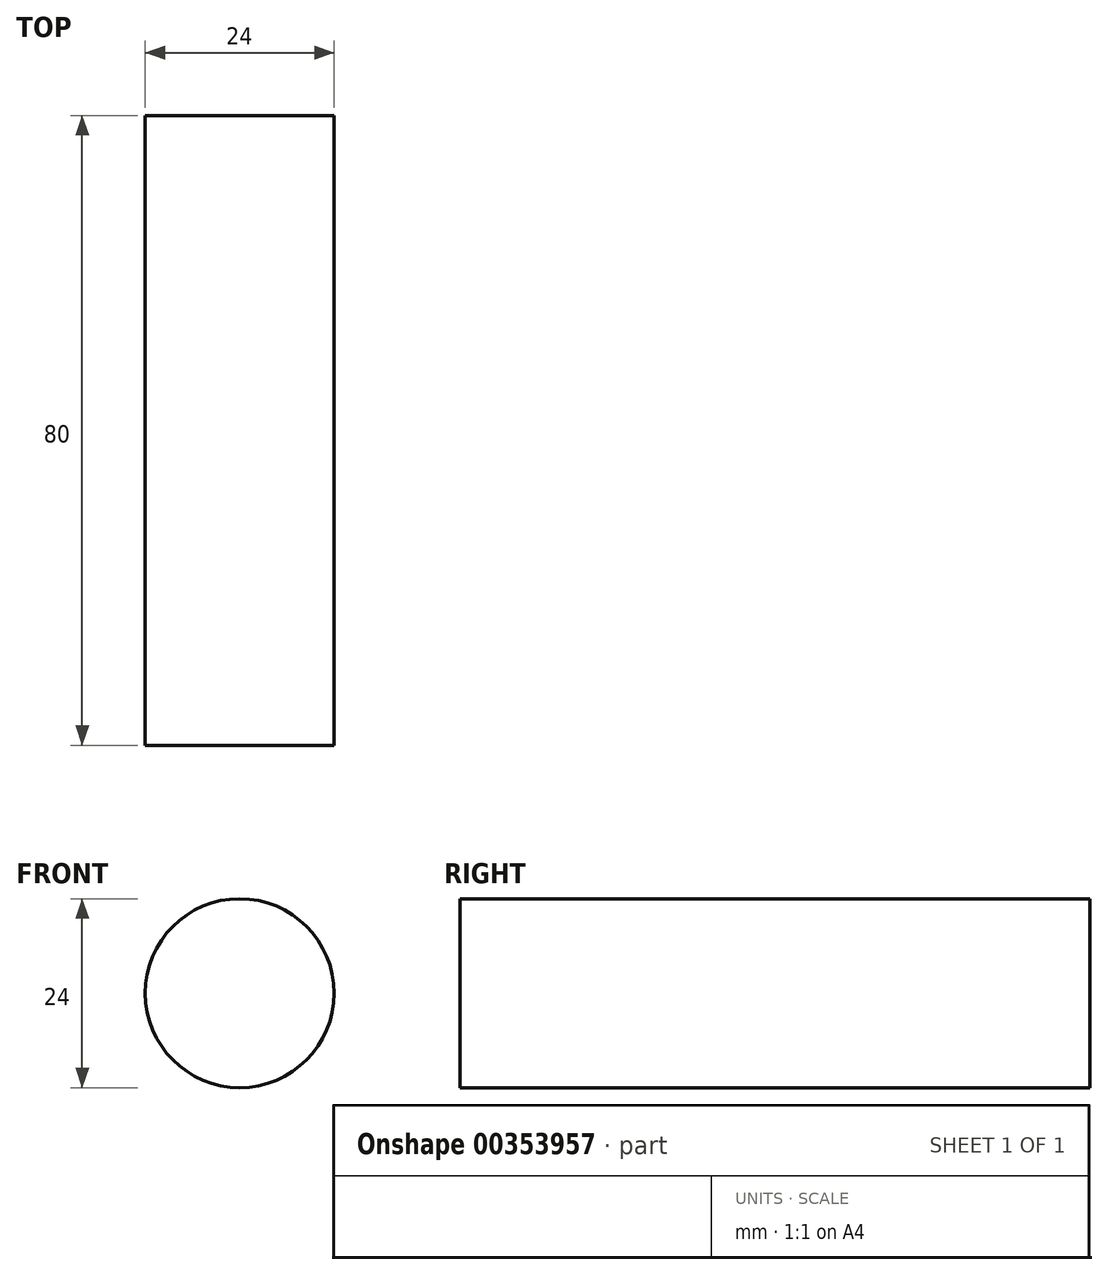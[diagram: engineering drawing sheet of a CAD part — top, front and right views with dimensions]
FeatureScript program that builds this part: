
annotation { "Feature Type Name" : "Feature", "Feature Type Description" : "" }
export const myFeature = defineFeature(function(context is Context, id is Id, definition is map)
    precondition{}
    {
        {
            var Q0;
            Q0=qCreatedBy(makeId("Front.planeOp"),FACE);
            var sketch = newSketch(context, id + "F0", { "sketchPlane" : qUnion([Q0])});
            skCircle(sketch, "E0", {"center": v(0, 0) * mm, "radius": 12 * mm});
            skSolve(sketch);
        }
        {
            var Q0;
            Q0=makeQuery(id+"F0.imprint","IMPRINT",FACE,{"disambiguationData":[TD([[makeQuery(id+"F0.imprint","IMPRINT",EDGE,{"derivedFrom":sQuery(id+"F0.wireOp",EDGE,"E0")}),1.0]])]});
            extrude(context, id + "F1", {"entities" : qUnion([Q0]), "endBound" : BoundingType.SYMMETRIC, "depth" : 80 * mm});
        }
    });
